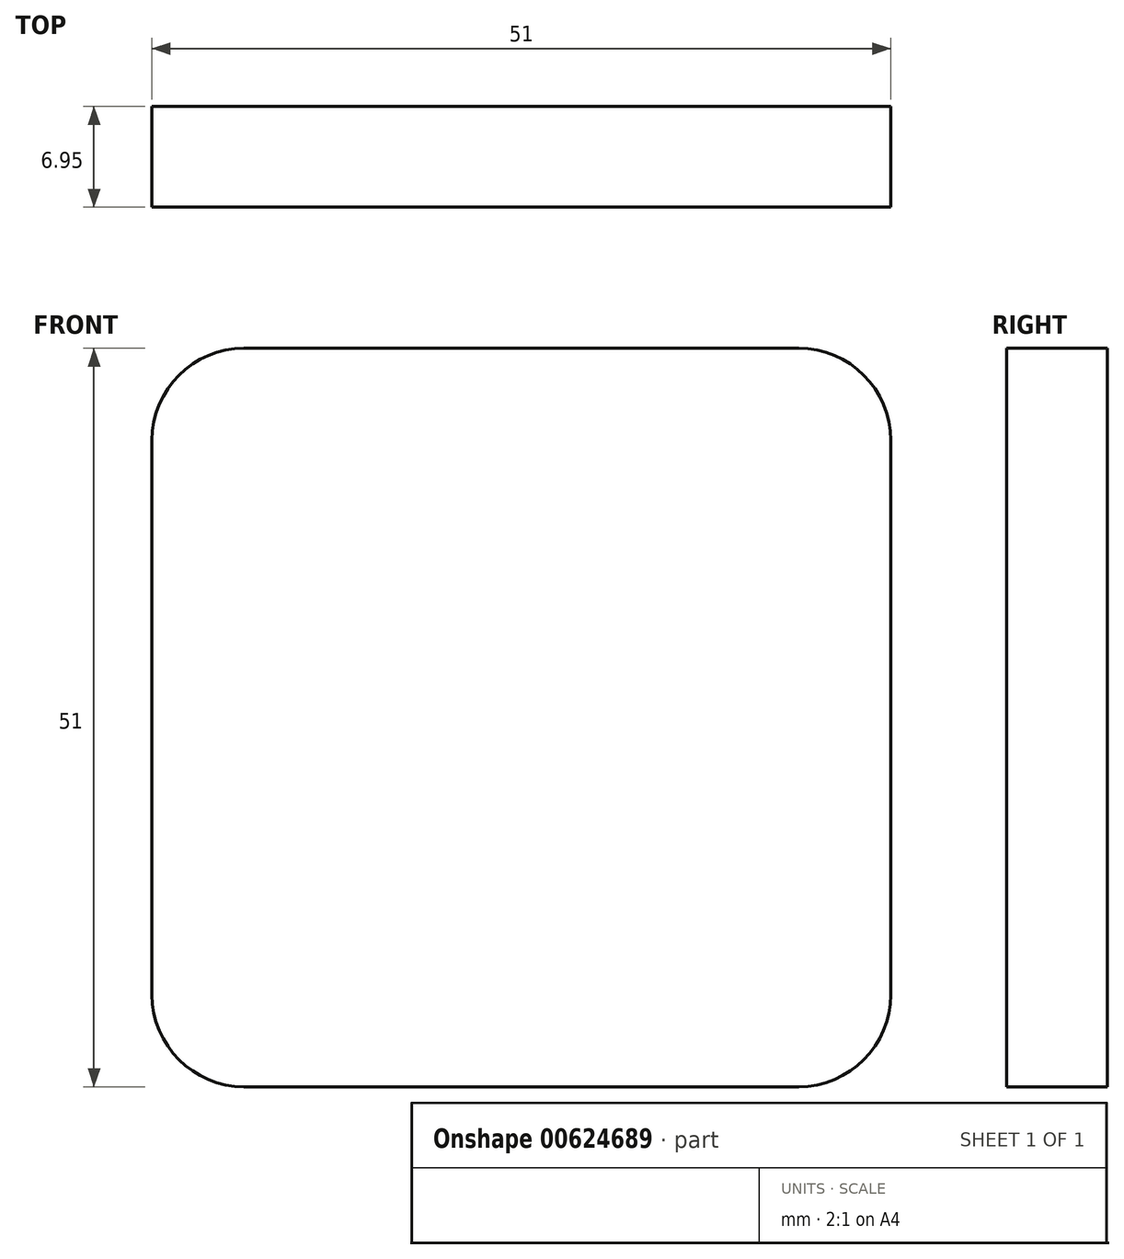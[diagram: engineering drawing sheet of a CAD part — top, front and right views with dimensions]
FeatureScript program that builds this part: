
annotation { "Feature Type Name" : "Feature", "Feature Type Description" : "" }
export const myFeature = defineFeature(function(context is Context, id is Id, definition is map)
    precondition{}
    {
        {
            var Q0;
            Q0=qCreatedBy(makeId("Front.planeOp"),FACE);
            var sketch = newSketch(context, id + "F0", { "sketchPlane" : qUnion([Q0])});
            skLineSegment(sketch, "E0.bottom", {"start": v(6.35, 0) * mm, "end": v(44.65, 0) * mm});
            skLineSegment(sketch, "E0.top", {"start": v(6.35, 51) * mm, "end": v(44.65, 51) * mm});
            skLineSegment(sketch, "E0.left", {"start": v(0, 6.35) * mm, "end": v(0, 44.65) * mm});
            skLineSegment(sketch, "E0.right", {"start": v(51, 6.35) * mm, "end": v(51, 44.65) * mm});
            skPoint(sketch, "E1.visualSharp", {"position": v(51, 51) * mm});
            skArc(sketch, "E1.filletArc", {"start": v(51, 44.65) * mm, "mid": v(49.14, 49.14) * mm, "end": v(44.65, 51) * mm});
            skPoint(sketch, "E2.visualSharp", {"position": v(0, 51) * mm});
            skArc(sketch, "E2.filletArc", {"start": v(6.35, 51) * mm, "mid": v(1.86, 49.14) * mm, "end": v(0, 44.65) * mm});
            skPoint(sketch, "E3.visualSharp", {"position": v(0, 0) * mm});
            skArc(sketch, "E3.filletArc", {"start": v(0, 6.35) * mm, "mid": v(1.86, 1.86) * mm, "end": v(6.35, 0) * mm});
            skPoint(sketch, "E4.visualSharp", {"position": v(51, 0) * mm});
            skArc(sketch, "E4.filletArc", {"start": v(44.65, 0) * mm, "mid": v(49.14, 1.86) * mm, "end": v(51, 6.35) * mm});
            skSolve(sketch);
        }
        {
            var Q0;
            Q0 = qSketchRegion(id + "F0", true);
            extrude(context, id + "F1", {"entities" : qUnion([Q0]), "depth" : 6.95 * mm, "offsetDistance" : 25.4 * mm});
        }
    });
